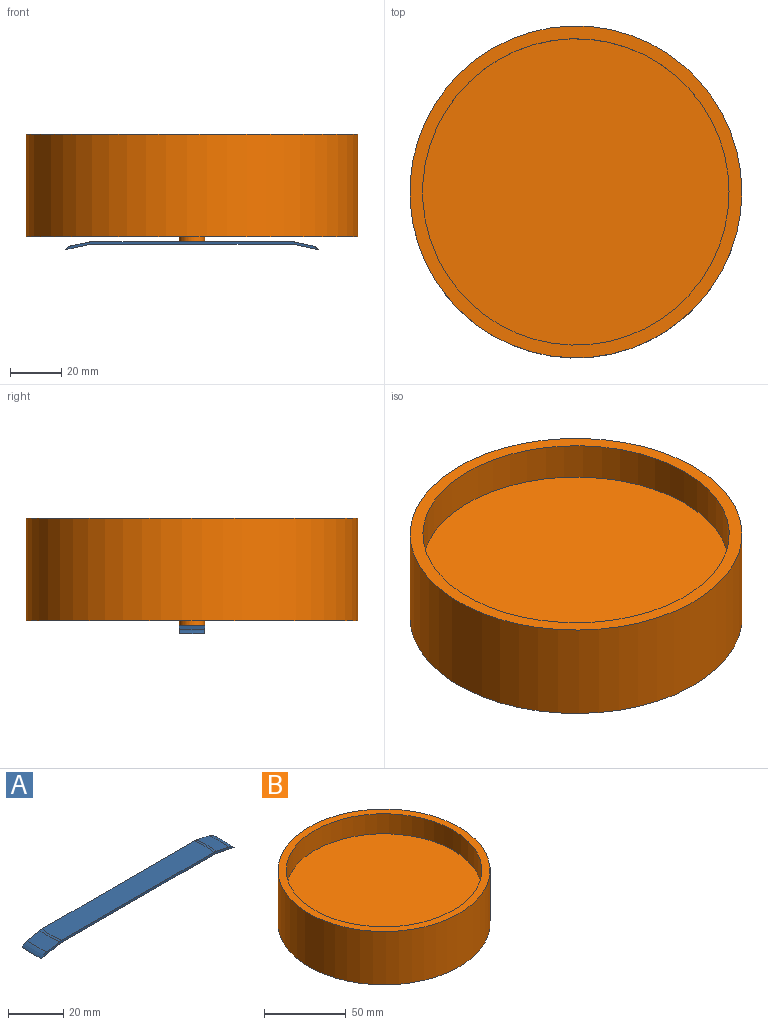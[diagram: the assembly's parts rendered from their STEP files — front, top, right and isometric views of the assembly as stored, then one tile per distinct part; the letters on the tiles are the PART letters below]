
ASSEMBLY  parts=2 mates=1
PART A: 12 faces, bbox 102.3x12.5x6.5 mm
  f0: plane 80x10mm, normal (0,0,-1), area 797.9mm2, adj f1,f2,f6,f7
  f1: cone r=40mm half-angle=78deg, axis (0,0,-1), area 98.8mm2, adj f0,f6,f7,f8
  f2: cone r=40mm half-angle=78deg, axis (0,0,-1), area 98.8mm2, adj f0,f6,f7,f10
  f3: cone r=49.78mm half-angle=78deg, axis (0,0,-1), area 65.1mm2, adj f6,f7,f10,f11
  f4: cone r=49.78mm half-angle=78deg, axis (0,0,-1), area 65.1mm2, adj f6,f7,f8,f9
  f5: plane 78.95x10mm, normal (0,0,1), area 787.4mm2, adj f6,f7,f9,f11
  f6: plane 98.76x3.17mm, normal (0,-1,0), area 99.1mm2, adj f0,f1,f2,f3,f4,f5,f8,f9
  f7: plane 98.76x3.17mm, normal (0,1,0), area 99.1mm2, adj f0,f1,f2,f3,f4,f5,f8,f9
  f8: torus R=45.81mm, axis (0,0,-1), area 32.3mm2, adj f1,f4,f6,f7
  f9: torus R=39.48mm, axis (0,0,-1), area 10.5mm2, adj f4,f5,f6,f7
  f10: torus R=45.81mm, axis (0,0,-1), area 32.3mm2, adj f2,f3,f6,f7
  f11: torus R=39.48mm, axis (0,0,-1), area 10.5mm2, adj f3,f5,f6,f7
PART B: 11 faces, bbox 130x130x42 mm
  f0: cylinder r=65mm len=130mm, axis (0,0,-1), area 16336.3mm2, adj f1,f2
  f1: plane 130x130mm, normal (0,0,1), area 1963.5mm2, adj f0,f3
  f2: plane 130x130mm, normal (0,0,-1), area 1963.5mm2, adj f0,f5
  f3: cylinder r=60mm len=120mm, axis (0,0,1), area 5654.9mm2, adj f1,f4
  f4: plane 120x120mm, normal (0,0,1), area 11309.7mm2, adj f3
  f5: cylinder r=60mm len=120mm, axis (0,0,-1), area 3769.9mm2, adj f2,f6
  f6: plane 120x120mm, normal (0,0,-1), area 9346.2mm2, adj f5,f8
  f7: plane 30.92x30.92mm, normal (0,0,-1), area 672.4mm2, adj f8,f9
  f8: torus R=15.46mm, axis (0,0,1), area 1669.7mm2, adj f6,f7
  f9: cylinder r=5mm len=10mm, axis (0,0,1), area 157.1mm2, adj f7,f10
  f10: plane 10x10mm, normal (0,0,-1), area 78.5mm2, adj f9
PLACE A t=(25.81,10.45,-24.29)mm
PLACE B t=(25.81,10.45,-21.27)mm
MATE revolute B.f9 <-> A.f1  axis (0,0,-1) through (25.81,10.45,-23.27)mm
